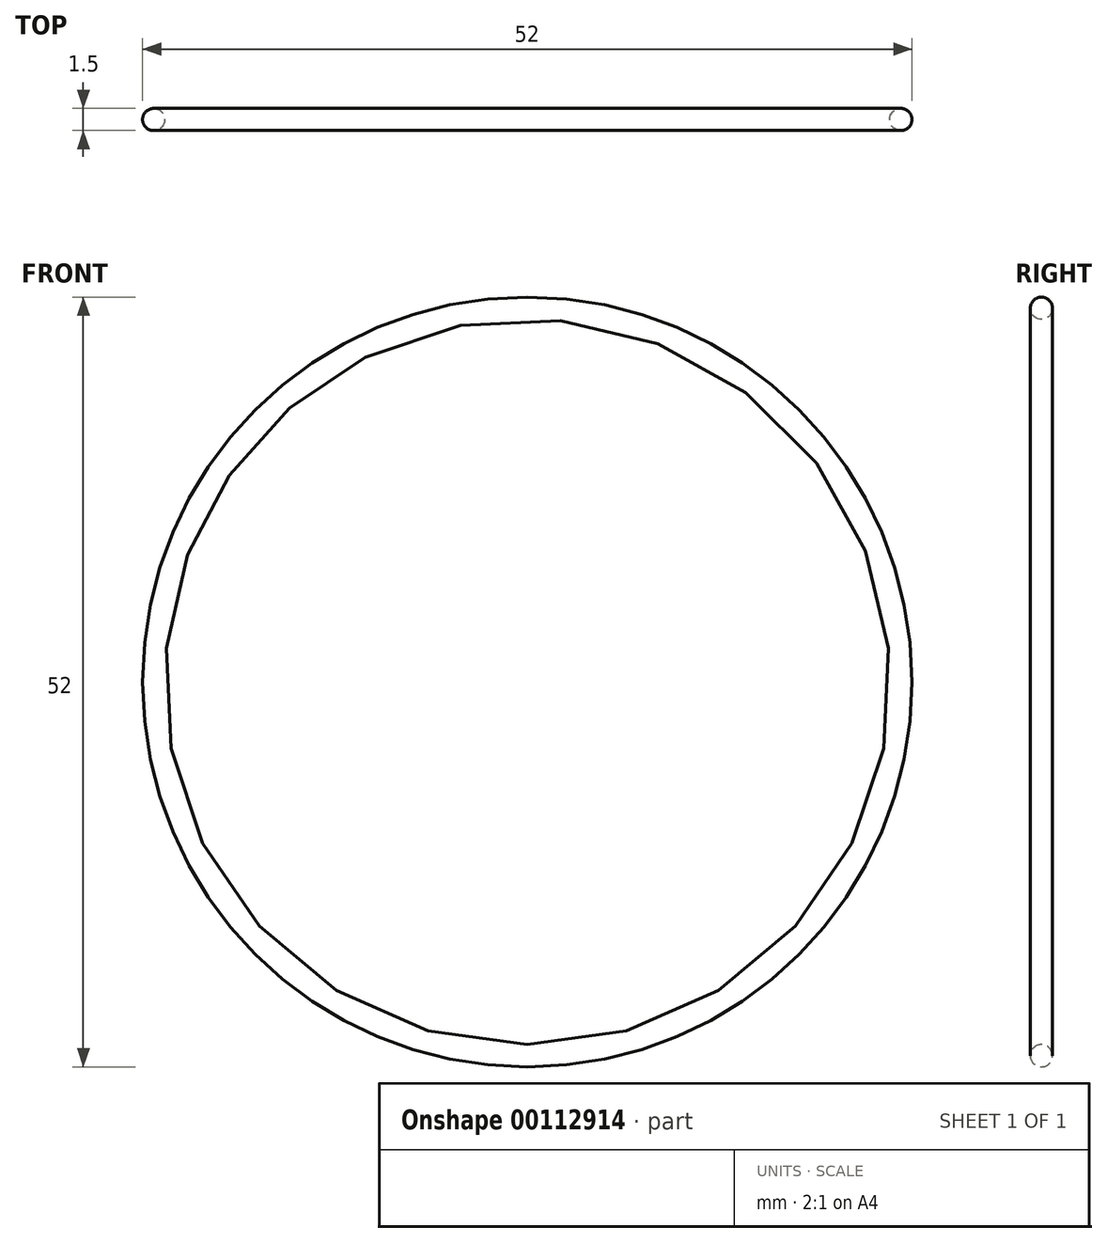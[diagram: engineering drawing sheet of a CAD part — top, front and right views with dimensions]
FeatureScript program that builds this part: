
annotation { "Feature Type Name" : "Feature", "Feature Type Description" : "" }
export const myFeature = defineFeature(function(context is Context, id is Id, definition is map)
    precondition{}
    {
        {
            var Q0;
            Q0=qCreatedBy(makeId("Right.planeOp"),FACE);
            var sketch = newSketch(context, id + "F0", { "sketchPlane" : qUnion([Q0])});
            skCircle(sketch, "E0", {"center": v(0, 25.25) * mm, "radius": 0.75 * mm});
            skLineSegment(sketch, "E1", {"start": v(-3.16, 0) * mm, "end": v(6.02, 0) * mm});
            skSolve(sketch);
        }
        {
            var Q0;
            Q0 = qSketchRegion(id + "F0", true);
            var Q1;
            Q1=sQuery(id+"F0.wireOp",EDGE,"E1");
            revolve(context, id + "F1", {"entities" : qUnion([Q0]), "axis" : qUnion([Q1]), "revolveType" : RevolveType.FULL});
        }
    });
